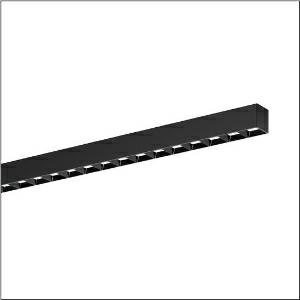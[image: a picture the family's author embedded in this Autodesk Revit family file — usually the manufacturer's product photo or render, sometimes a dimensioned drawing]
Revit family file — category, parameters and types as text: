
# Revit family: silica_21_51mx22tctab
name_source: partatom
category: Lighting Fixtures
units: mm (PartAtom-declared; Revit-internal decimal feet)

## family parameters
Cut with Voids When Loaded = No
Host = Face
Light Source = No
Part Type = Normal
Room Calculation Point = No
Round Connector Dimension = Use Diameter
Shared = No

## types (1)
- --- (1 x LED, 9300 lm, 80.4 W, 6500K)
    Apparent Load = 80 VA
    CIE Flux Codes = 84 100 100 100 100
    Color Rendering = 80
    Color Temperature = 6500K
    Default Elevation = 1800 mm
    Description = Silica 21, office luminaire, primary light control with darklight reflector, of PMMA, black, CAT 2 (L<= 3000cd/m²), light emission: direct distribution, primary light characteristic: symmetric, installation type: surface-mounted, LED, rated luminous flux: 9.300lm, luminous efficacy: 110lm/W, light colour: 8tw, colour temperature: 2700..6500K, control gear: DALI DT8, with terminal, 3+2-pole, max. 2.5mm², mains connection: 220..240V, AC, 50/60Hz, rated input power: 84.5W, luminaire housing, of aluminium, matt jet black (RAL 9005), length: 3.004mm, width: 53mm, height: 53mm, protection rating (complete): IP20, insulation class (complete): insulation class I (protective earthing), certification: CE, permissible operating ambient temperature: 0..+35°C, standard: EN 50419, packaging unit: 1 piece
    Height = 53 mm
    Lamp = 1 x LED
    Lamp Light Flux = 9300 lm
    Lamp Power = 80.4 W
    Lamp count = 1
    Length = 3004 mm
    Luminous efficacy = 116 lm/W
    Manufacturer = Siteco
    ModVariant = No
    Model = 51MX22TCTAB
    Mounting Place = Ceiling
    Mounting Type = Surface mounted
    Number of Poles = 1
    OnlyDefault = Yes
    Power Factor = 1
    Product Name = Silica 21
    Product group = office luminaire | ceiling mounted
    ProductGroupID = 301
    Protection Class = Protection class I
    Protection Degree = IP 20
    RLX_Detail_Level = 1
    RLX_Emergency_Light_Flux = 0 lm
    RLX_Emergency_Type = 0
    RLX_Emergency_Type_DB = No
    RlxData = <blob elided: 61549 chars, md5=81eb13c6>
    Socket = socket
    Standby Power = 0 W
    System Light Flux = 9300 lm
    System Power = 80 W
    Type Comments = individual setting
    Type Image = l_1335908.jpg
    URL = http://relux.com
    VarID = @adj_139625
    Voltage = 0 V
    Weight = 0.00 kg
    Width = 53 mm

## geometry (parser evidence)
native form markers: Blend x4, Sweep x12
no freeform markers — native parametric forms only
